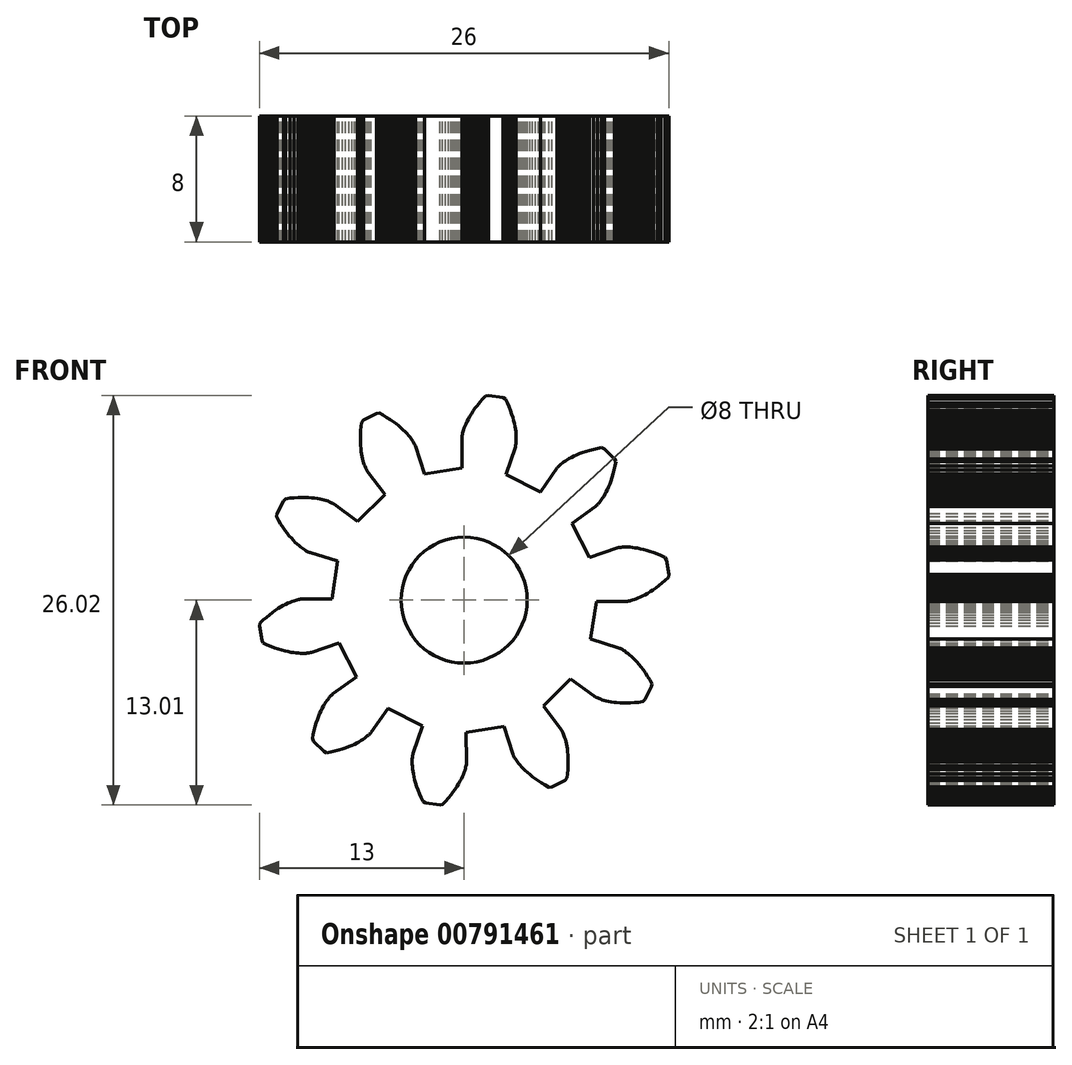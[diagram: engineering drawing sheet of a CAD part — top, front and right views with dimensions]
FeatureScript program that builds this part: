
annotation { "Feature Type Name" : "Feature", "Feature Type Description" : "" }
export const myFeature = defineFeature(function(context is Context, id is Id, definition is map)
    precondition{}
    {
        {
            var Q0;
            Q0=qCreatedBy(makeId("Front.planeOp"),FACE);
            var sketch = newSketch(context, id + "F0", { "sketchPlane" : qUnion([Q0])});
            skCircle(sketch, "E0", {"center": v(0, 0) * mm, "radius": 4 * mm});
            skLineSegment(sketch, "E1", {"start": v(-8.4, 0.07) * mm, "end": v(-10.26, 0.08) * mm});
            skLineSegment(sketch, "E2", {"start": v(-10.26, 0.08) * mm, "end": v(-10.27, 0.08) * mm});
            skLineSegment(sketch, "E3", {"start": v(-10.27, 0.08) * mm, "end": v(-10.3, 0.08) * mm});
            skLineSegment(sketch, "E4", {"start": v(-10.3, 0.08) * mm, "end": v(-10.33, 0.08) * mm});
            skLineSegment(sketch, "E5", {"start": v(-10.33, 0.08) * mm, "end": v(-10.38, 0.07) * mm});
            skLineSegment(sketch, "E6", {"start": v(-10.38, 0.07) * mm, "end": v(-10.45, 0.06) * mm});
            skLineSegment(sketch, "E7", {"start": v(-10.45, 0.06) * mm, "end": v(-10.52, 0.04) * mm});
            skLineSegment(sketch, "E8", {"start": v(-10.52, 0.04) * mm, "end": v(-10.6, 0.02) * mm});
            skLineSegment(sketch, "E9", {"start": v(-10.6, 0.02) * mm, "end": v(-10.7, 0) * mm});
            skLineSegment(sketch, "E10", {"start": v(-10.7, 0) * mm, "end": v(-10.8, -0.04) * mm});
            skLineSegment(sketch, "E11", {"start": v(-10.8, -0.04) * mm, "end": v(-10.93, -0.08) * mm});
            skLineSegment(sketch, "E12", {"start": v(-10.93, -0.08) * mm, "end": v(-11.05, -0.13) * mm});
            skLineSegment(sketch, "E13", {"start": v(-11.05, -0.13) * mm, "end": v(-11.2, -0.2) * mm});
            skLineSegment(sketch, "E14", {"start": v(-11.2, -0.2) * mm, "end": v(-11.34, -0.26) * mm});
            skLineSegment(sketch, "E15", {"start": v(-11.34, -0.26) * mm, "end": v(-11.5, -0.34) * mm});
            skLineSegment(sketch, "E16", {"start": v(-11.5, -0.34) * mm, "end": v(-11.66, -0.43) * mm});
            skLineSegment(sketch, "E17", {"start": v(-11.66, -0.43) * mm, "end": v(-11.83, -0.54) * mm});
            skLineSegment(sketch, "E18", {"start": v(-11.83, -0.54) * mm, "end": v(-12, -0.66) * mm});
            skLineSegment(sketch, "E19", {"start": v(-12, -0.66) * mm, "end": v(-12.19, -0.79) * mm});
            skLineSegment(sketch, "E20", {"start": v(-12.19, -0.79) * mm, "end": v(-12.37, -0.93) * mm});
            skLineSegment(sketch, "E21", {"start": v(-12.37, -0.93) * mm, "end": v(-12.57, -1.1) * mm});
            skLineSegment(sketch, "E22", {"start": v(-12.57, -1.1) * mm, "end": v(-12.76, -1.26) * mm});
            skLineSegment(sketch, "E23", {"start": v(-12.76, -1.26) * mm, "end": v(-12.96, -1.45) * mm});
            skLineSegment(sketch, "E24", {"start": v(-12.96, -1.45) * mm, "end": v(-13, -1.64) * mm});
            skLineSegment(sketch, "E25", {"start": v(-13, -1.64) * mm, "end": v(-12.85, -2.55) * mm});
            skLineSegment(sketch, "E26", {"start": v(-12.85, -2.55) * mm, "end": v(-12.76, -2.71) * mm});
            skLineSegment(sketch, "E27", {"start": v(-12.76, -2.71) * mm, "end": v(-12.51, -2.83) * mm});
            skLineSegment(sketch, "E28", {"start": v(-12.51, -2.83) * mm, "end": v(-12.27, -2.93) * mm});
            skLineSegment(sketch, "E29", {"start": v(-12.27, -2.93) * mm, "end": v(-12.04, -3.02) * mm});
            skLineSegment(sketch, "E30", {"start": v(-12.04, -3.02) * mm, "end": v(-11.81, -3.1) * mm});
            skLineSegment(sketch, "E31", {"start": v(-11.81, -3.1) * mm, "end": v(-11.6, -3.17) * mm});
            skLineSegment(sketch, "E32", {"start": v(-11.6, -3.17) * mm, "end": v(-11.4, -3.22) * mm});
            skLineSegment(sketch, "E33", {"start": v(-11.4, -3.22) * mm, "end": v(-11.2, -3.27) * mm});
            skLineSegment(sketch, "E34", {"start": v(-11.2, -3.27) * mm, "end": v(-11.01, -3.3) * mm});
            skLineSegment(sketch, "E35", {"start": v(-11.01, -3.3) * mm, "end": v(-10.84, -3.33) * mm});
            skLineSegment(sketch, "E36", {"start": v(-10.84, -3.33) * mm, "end": v(-10.68, -3.35) * mm});
            skLineSegment(sketch, "E37", {"start": v(-10.68, -3.35) * mm, "end": v(-10.53, -3.37) * mm});
            skLineSegment(sketch, "E38", {"start": v(-10.53, -3.37) * mm, "end": v(-10.4, -3.37) * mm});
            skLineSegment(sketch, "E39", {"start": v(-10.4, -3.37) * mm, "end": v(-10.27, -3.38) * mm});
            skLineSegment(sketch, "E40", {"start": v(-10.27, -3.38) * mm, "end": v(-10.15, -3.37) * mm});
            skLineSegment(sketch, "E41", {"start": v(-10.15, -3.37) * mm, "end": v(-10.05, -3.37) * mm});
            skLineSegment(sketch, "E42", {"start": v(-10.05, -3.37) * mm, "end": v(-9.97, -3.36) * mm});
            skLineSegment(sketch, "E43", {"start": v(-9.97, -3.36) * mm, "end": v(-9.9, -3.35) * mm});
            skLineSegment(sketch, "E44", {"start": v(-9.9, -3.35) * mm, "end": v(-9.83, -3.34) * mm});
            skLineSegment(sketch, "E45", {"start": v(-9.83, -3.34) * mm, "end": v(-9.78, -3.33) * mm});
            skLineSegment(sketch, "E46", {"start": v(-9.78, -3.33) * mm, "end": v(-9.75, -3.33) * mm});
            skLineSegment(sketch, "E47", {"start": v(-9.75, -3.33) * mm, "end": v(-9.72, -3.32) * mm});
            skLineSegment(sketch, "E48", {"start": v(-9.72, -3.32) * mm, "end": v(-9.7, -3.32) * mm});
            skLineSegment(sketch, "E49", {"start": v(-9.7, -3.32) * mm, "end": v(-7.95, -2.72) * mm});
            skLineSegment(sketch, "E50", {"start": v(-7.95, -2.72) * mm, "end": v(-6.84, -4.89) * mm});
            skLineSegment(sketch, "E51", {"start": v(-6.84, -4.89) * mm, "end": v(-8.35, -5.96) * mm});
            skLineSegment(sketch, "E52", {"start": v(-8.35, -5.96) * mm, "end": v(-8.36, -5.97) * mm});
            skLineSegment(sketch, "E53", {"start": v(-8.36, -5.97) * mm, "end": v(-8.38, -5.99) * mm});
            skLineSegment(sketch, "E54", {"start": v(-8.38, -5.99) * mm, "end": v(-8.4, -6.01) * mm});
            skLineSegment(sketch, "E55", {"start": v(-8.4, -6.01) * mm, "end": v(-8.44, -6.05) * mm});
            skLineSegment(sketch, "E56", {"start": v(-8.44, -6.05) * mm, "end": v(-8.48, -6.1) * mm});
            skLineSegment(sketch, "E57", {"start": v(-8.48, -6.1) * mm, "end": v(-8.54, -6.15) * mm});
            skLineSegment(sketch, "E58", {"start": v(-8.54, -6.15) * mm, "end": v(-8.6, -6.21) * mm});
            skLineSegment(sketch, "E59", {"start": v(-8.6, -6.21) * mm, "end": v(-8.65, -6.3) * mm});
            skLineSegment(sketch, "E60", {"start": v(-8.65, -6.3) * mm, "end": v(-8.72, -6.38) * mm});
            skLineSegment(sketch, "E61", {"start": v(-8.72, -6.38) * mm, "end": v(-8.8, -6.49) * mm});
            skLineSegment(sketch, "E62", {"start": v(-8.8, -6.49) * mm, "end": v(-8.87, -6.6) * mm});
            skLineSegment(sketch, "E63", {"start": v(-8.87, -6.6) * mm, "end": v(-8.94, -6.73) * mm});
            skLineSegment(sketch, "E64", {"start": v(-8.94, -6.73) * mm, "end": v(-9.02, -6.87) * mm});
            skLineSegment(sketch, "E65", {"start": v(-9.02, -6.87) * mm, "end": v(-9.1, -7.03) * mm});
            skLineSegment(sketch, "E66", {"start": v(-9.1, -7.03) * mm, "end": v(-9.17, -7.2) * mm});
            skLineSegment(sketch, "E67", {"start": v(-9.17, -7.2) * mm, "end": v(-9.25, -7.39) * mm});
            skLineSegment(sketch, "E68", {"start": v(-9.25, -7.39) * mm, "end": v(-9.33, -7.59) * mm});
            skLineSegment(sketch, "E69", {"start": v(-9.33, -7.59) * mm, "end": v(-9.4, -7.8) * mm});
            skLineSegment(sketch, "E70", {"start": v(-9.4, -7.8) * mm, "end": v(-9.46, -8.03) * mm});
            skLineSegment(sketch, "E71", {"start": v(-9.46, -8.03) * mm, "end": v(-9.53, -8.27) * mm});
            skLineSegment(sketch, "E72", {"start": v(-9.53, -8.27) * mm, "end": v(-9.58, -8.53) * mm});
            skLineSegment(sketch, "E73", {"start": v(-9.58, -8.53) * mm, "end": v(-9.63, -8.8) * mm});
            skLineSegment(sketch, "E74", {"start": v(-9.63, -8.8) * mm, "end": v(-9.55, -8.97) * mm});
            skLineSegment(sketch, "E75", {"start": v(-9.55, -8.97) * mm, "end": v(-8.9, -9.61) * mm});
            skLineSegment(sketch, "E76", {"start": v(-8.9, -9.61) * mm, "end": v(-8.73, -9.7) * mm});
            skLineSegment(sketch, "E77", {"start": v(-8.73, -9.7) * mm, "end": v(-8.46, -9.64) * mm});
            skLineSegment(sketch, "E78", {"start": v(-8.46, -9.64) * mm, "end": v(-8.2, -9.58) * mm});
            skLineSegment(sketch, "E79", {"start": v(-8.2, -9.58) * mm, "end": v(-7.96, -9.52) * mm});
            skLineSegment(sketch, "E80", {"start": v(-7.96, -9.52) * mm, "end": v(-7.73, -9.45) * mm});
            skLineSegment(sketch, "E81", {"start": v(-7.73, -9.45) * mm, "end": v(-7.52, -9.38) * mm});
            skLineSegment(sketch, "E82", {"start": v(-7.52, -9.38) * mm, "end": v(-7.32, -9.3) * mm});
            skLineSegment(sketch, "E83", {"start": v(-7.32, -9.3) * mm, "end": v(-7.14, -9.22) * mm});
            skLineSegment(sketch, "E84", {"start": v(-7.14, -9.22) * mm, "end": v(-6.97, -9.15) * mm});
            skLineSegment(sketch, "E85", {"start": v(-6.97, -9.15) * mm, "end": v(-6.81, -9.07) * mm});
            skLineSegment(sketch, "E86", {"start": v(-6.81, -9.07) * mm, "end": v(-6.67, -8.99) * mm});
            skLineSegment(sketch, "E87", {"start": v(-6.67, -8.99) * mm, "end": v(-6.54, -8.91) * mm});
            skLineSegment(sketch, "E88", {"start": v(-6.54, -8.91) * mm, "end": v(-6.42, -8.84) * mm});
            skLineSegment(sketch, "E89", {"start": v(-6.42, -8.84) * mm, "end": v(-6.32, -8.77) * mm});
            skLineSegment(sketch, "E90", {"start": v(-6.32, -8.77) * mm, "end": v(-6.23, -8.7) * mm});
            skLineSegment(sketch, "E91", {"start": v(-6.23, -8.7) * mm, "end": v(-6.15, -8.64) * mm});
            skLineSegment(sketch, "E92", {"start": v(-6.15, -8.64) * mm, "end": v(-6.09, -8.58) * mm});
            skLineSegment(sketch, "E93", {"start": v(-6.09, -8.58) * mm, "end": v(-6.03, -8.53) * mm});
            skLineSegment(sketch, "E94", {"start": v(-6.03, -8.53) * mm, "end": v(-5.99, -8.48) * mm});
            skLineSegment(sketch, "E95", {"start": v(-5.99, -8.48) * mm, "end": v(-5.95, -8.45) * mm});
            skLineSegment(sketch, "E96", {"start": v(-5.95, -8.45) * mm, "end": v(-5.93, -8.42) * mm});
            skLineSegment(sketch, "E97", {"start": v(-5.93, -8.42) * mm, "end": v(-5.91, -8.4) * mm});
            skLineSegment(sketch, "E98", {"start": v(-5.91, -8.4) * mm, "end": v(-5.9, -8.39) * mm});
            skLineSegment(sketch, "E99", {"start": v(-5.9, -8.39) * mm, "end": v(-4.84, -6.87) * mm});
            skLineSegment(sketch, "E100", {"start": v(-4.84, -6.87) * mm, "end": v(-2.66, -7.97) * mm});
            skLineSegment(sketch, "E101", {"start": v(-2.66, -7.97) * mm, "end": v(-3.25, -9.73) * mm});
            skLineSegment(sketch, "E102", {"start": v(-3.25, -9.73) * mm, "end": v(-3.25, -9.74) * mm});
            skLineSegment(sketch, "E103", {"start": v(-3.25, -9.74) * mm, "end": v(-3.26, -9.77) * mm});
            skLineSegment(sketch, "E104", {"start": v(-3.26, -9.77) * mm, "end": v(-3.27, -9.8) * mm});
            skLineSegment(sketch, "E105", {"start": v(-3.27, -9.8) * mm, "end": v(-3.27, -9.85) * mm});
            skLineSegment(sketch, "E106", {"start": v(-3.27, -9.85) * mm, "end": v(-3.28, -9.92) * mm});
            skLineSegment(sketch, "E107", {"start": v(-3.28, -9.92) * mm, "end": v(-3.3, -10) * mm});
            skLineSegment(sketch, "E108", {"start": v(-3.3, -10) * mm, "end": v(-3.3, -10.08) * mm});
            skLineSegment(sketch, "E109", {"start": v(-3.3, -10.08) * mm, "end": v(-3.3, -10.18) * mm});
            skLineSegment(sketch, "E110", {"start": v(-3.3, -10.18) * mm, "end": v(-3.3, -10.3) * mm});
            skLineSegment(sketch, "E111", {"start": v(-3.3, -10.3) * mm, "end": v(-3.3, -10.42) * mm});
            skLineSegment(sketch, "E112", {"start": v(-3.3, -10.42) * mm, "end": v(-3.3, -10.55) * mm});
            skLineSegment(sketch, "E113", {"start": v(-3.3, -10.55) * mm, "end": v(-3.28, -10.7) * mm});
            skLineSegment(sketch, "E114", {"start": v(-3.28, -10.7) * mm, "end": v(-3.26, -10.86) * mm});
            skLineSegment(sketch, "E115", {"start": v(-3.26, -10.86) * mm, "end": v(-3.23, -11.04) * mm});
            skLineSegment(sketch, "E116", {"start": v(-3.23, -11.04) * mm, "end": v(-3.19, -11.22) * mm});
            skLineSegment(sketch, "E117", {"start": v(-3.19, -11.22) * mm, "end": v(-3.14, -11.41) * mm});
            skLineSegment(sketch, "E118", {"start": v(-3.14, -11.41) * mm, "end": v(-3.09, -11.62) * mm});
            skLineSegment(sketch, "E119", {"start": v(-3.09, -11.62) * mm, "end": v(-3.02, -11.83) * mm});
            skLineSegment(sketch, "E120", {"start": v(-3.02, -11.83) * mm, "end": v(-2.94, -12.06) * mm});
            skLineSegment(sketch, "E121", {"start": v(-2.94, -12.06) * mm, "end": v(-2.85, -12.29) * mm});
            skLineSegment(sketch, "E122", {"start": v(-2.85, -12.29) * mm, "end": v(-2.74, -12.53) * mm});
            skLineSegment(sketch, "E123", {"start": v(-2.74, -12.53) * mm, "end": v(-2.62, -12.78) * mm});
            skLineSegment(sketch, "E124", {"start": v(-2.62, -12.78) * mm, "end": v(-2.46, -12.87) * mm});
            skLineSegment(sketch, "E125", {"start": v(-2.46, -12.87) * mm, "end": v(-1.55, -13) * mm});
            skLineSegment(sketch, "E126", {"start": v(-1.55, -13) * mm, "end": v(-1.36, -12.97) * mm});
            skLineSegment(sketch, "E127", {"start": v(-1.36, -12.97) * mm, "end": v(-1.18, -12.77) * mm});
            skLineSegment(sketch, "E128", {"start": v(-1.18, -12.77) * mm, "end": v(-1, -12.57) * mm});
            skLineSegment(sketch, "E129", {"start": v(-1, -12.57) * mm, "end": v(-0.84, -12.38) * mm});
            skLineSegment(sketch, "E130", {"start": v(-0.84, -12.38) * mm, "end": v(-0.7, -12.2) * mm});
            skLineSegment(sketch, "E131", {"start": v(-0.7, -12.2) * mm, "end": v(-0.57, -12) * mm});
            skLineSegment(sketch, "E132", {"start": v(-0.57, -12) * mm, "end": v(-0.46, -11.83) * mm});
            skLineSegment(sketch, "E133", {"start": v(-0.46, -11.83) * mm, "end": v(-0.35, -11.66) * mm});
            skLineSegment(sketch, "E134", {"start": v(-0.35, -11.66) * mm, "end": v(-0.26, -11.5) * mm});
            skLineSegment(sketch, "E135", {"start": v(-0.26, -11.5) * mm, "end": v(-0.18, -11.34) * mm});
            skLineSegment(sketch, "E136", {"start": v(-0.18, -11.34) * mm, "end": v(-0.11, -11.2) * mm});
            skLineSegment(sketch, "E137", {"start": v(-0.11, -11.2) * mm, "end": v(-0.05, -11.05) * mm});
            skLineSegment(sketch, "E138", {"start": v(-0.05, -11.05) * mm, "end": v(0, -10.93) * mm});
            skLineSegment(sketch, "E139", {"start": v(0, -10.93) * mm, "end": v(0.04, -10.8) * mm});
            skLineSegment(sketch, "E140", {"start": v(0.04, -10.8) * mm, "end": v(0.07, -10.7) * mm});
            skLineSegment(sketch, "E141", {"start": v(0.07, -10.7) * mm, "end": v(0.1, -10.6) * mm});
            skLineSegment(sketch, "E142", {"start": v(0.1, -10.6) * mm, "end": v(0.12, -10.52) * mm});
            skLineSegment(sketch, "E143", {"start": v(0.12, -10.52) * mm, "end": v(0.13, -10.44) * mm});
            skLineSegment(sketch, "E144", {"start": v(0.13, -10.44) * mm, "end": v(0.14, -10.38) * mm});
            skLineSegment(sketch, "E145", {"start": v(0.14, -10.38) * mm, "end": v(0.15, -10.33) * mm});
            skLineSegment(sketch, "E146", {"start": v(0.15, -10.33) * mm, "end": v(0.15, -10.3) * mm});
            skLineSegment(sketch, "E147", {"start": v(0.15, -10.3) * mm, "end": v(0.15, -10.27) * mm});
            skLineSegment(sketch, "E148", {"start": v(0.15, -10.27) * mm, "end": v(0.15, -10.26) * mm});
            skLineSegment(sketch, "E149", {"start": v(0.15, -10.26) * mm, "end": v(0.13, -8.4) * mm});
            skLineSegment(sketch, "E150", {"start": v(0.13, -8.4) * mm, "end": v(2.53, -8.01) * mm});
            skLineSegment(sketch, "E151", {"start": v(2.53, -8.01) * mm, "end": v(3.1, -9.78) * mm});
            skLineSegment(sketch, "E152", {"start": v(3.1, -9.78) * mm, "end": v(3.1, -9.8) * mm});
            skLineSegment(sketch, "E153", {"start": v(3.1, -9.8) * mm, "end": v(3.1, -9.82) * mm});
            skLineSegment(sketch, "E154", {"start": v(3.1, -9.82) * mm, "end": v(3.12, -9.85) * mm});
            skLineSegment(sketch, "E155", {"start": v(3.12, -9.85) * mm, "end": v(3.14, -9.9) * mm});
            skLineSegment(sketch, "E156", {"start": v(3.14, -9.9) * mm, "end": v(3.17, -9.95) * mm});
            skLineSegment(sketch, "E157", {"start": v(3.17, -9.95) * mm, "end": v(3.2, -10.02) * mm});
            skLineSegment(sketch, "E158", {"start": v(3.2, -10.02) * mm, "end": v(3.26, -10.1) * mm});
            skLineSegment(sketch, "E159", {"start": v(3.26, -10.1) * mm, "end": v(3.31, -10.18) * mm});
            skLineSegment(sketch, "E160", {"start": v(3.31, -10.18) * mm, "end": v(3.38, -10.27) * mm});
            skLineSegment(sketch, "E161", {"start": v(3.38, -10.27) * mm, "end": v(3.45, -10.37) * mm});
            skLineSegment(sketch, "E162", {"start": v(3.45, -10.37) * mm, "end": v(3.54, -10.47) * mm});
            skLineSegment(sketch, "E163", {"start": v(3.54, -10.47) * mm, "end": v(3.64, -10.58) * mm});
            skLineSegment(sketch, "E164", {"start": v(3.64, -10.58) * mm, "end": v(3.75, -10.7) * mm});
            skLineSegment(sketch, "E165", {"start": v(3.75, -10.7) * mm, "end": v(3.88, -10.82) * mm});
            skLineSegment(sketch, "E166", {"start": v(3.88, -10.82) * mm, "end": v(4.01, -10.95) * mm});
            skLineSegment(sketch, "E167", {"start": v(4.01, -10.95) * mm, "end": v(4.17, -11.08) * mm});
            skLineSegment(sketch, "E168", {"start": v(4.17, -11.08) * mm, "end": v(4.33, -11.21) * mm});
            skLineSegment(sketch, "E169", {"start": v(4.33, -11.21) * mm, "end": v(4.51, -11.35) * mm});
            skLineSegment(sketch, "E170", {"start": v(4.51, -11.35) * mm, "end": v(4.7, -11.48) * mm});
            skLineSegment(sketch, "E171", {"start": v(4.7, -11.48) * mm, "end": v(4.92, -11.61) * mm});
            skLineSegment(sketch, "E172", {"start": v(4.92, -11.61) * mm, "end": v(5.15, -11.75) * mm});
            skLineSegment(sketch, "E173", {"start": v(5.15, -11.75) * mm, "end": v(5.39, -11.88) * mm});
            skLineSegment(sketch, "E174", {"start": v(5.39, -11.88) * mm, "end": v(5.57, -11.85) * mm});
            skLineSegment(sketch, "E175", {"start": v(5.57, -11.85) * mm, "end": v(6.4, -11.43) * mm});
            skLineSegment(sketch, "E176", {"start": v(6.4, -11.43) * mm, "end": v(6.52, -11.3) * mm});
            skLineSegment(sketch, "E177", {"start": v(6.52, -11.3) * mm, "end": v(6.56, -11.02) * mm});
            skLineSegment(sketch, "E178", {"start": v(6.56, -11.02) * mm, "end": v(6.58, -10.76) * mm});
            skLineSegment(sketch, "E179", {"start": v(6.58, -10.76) * mm, "end": v(6.6, -10.51) * mm});
            skLineSegment(sketch, "E180", {"start": v(6.6, -10.51) * mm, "end": v(6.6, -10.28) * mm});
            skLineSegment(sketch, "E181", {"start": v(6.6, -10.28) * mm, "end": v(6.6, -10.05) * mm});
            skLineSegment(sketch, "E182", {"start": v(6.6, -10.05) * mm, "end": v(6.58, -9.84) * mm});
            skLineSegment(sketch, "E183", {"start": v(6.58, -9.84) * mm, "end": v(6.57, -9.64) * mm});
            skLineSegment(sketch, "E184", {"start": v(6.57, -9.64) * mm, "end": v(6.55, -9.45) * mm});
            skLineSegment(sketch, "E185", {"start": v(6.55, -9.45) * mm, "end": v(6.52, -9.28) * mm});
            skLineSegment(sketch, "E186", {"start": v(6.52, -9.28) * mm, "end": v(6.49, -9.12) * mm});
            skLineSegment(sketch, "E187", {"start": v(6.49, -9.12) * mm, "end": v(6.45, -8.97) * mm});
            skLineSegment(sketch, "E188", {"start": v(6.45, -8.97) * mm, "end": v(6.42, -8.84) * mm});
            skLineSegment(sketch, "E189", {"start": v(6.42, -8.84) * mm, "end": v(6.38, -8.72) * mm});
            skLineSegment(sketch, "E190", {"start": v(6.38, -8.72) * mm, "end": v(6.35, -8.61) * mm});
            skLineSegment(sketch, "E191", {"start": v(6.35, -8.61) * mm, "end": v(6.31, -8.52) * mm});
            skLineSegment(sketch, "E192", {"start": v(6.31, -8.52) * mm, "end": v(6.28, -8.44) * mm});
            skLineSegment(sketch, "E193", {"start": v(6.28, -8.44) * mm, "end": v(6.25, -8.37) * mm});
            skLineSegment(sketch, "E194", {"start": v(6.25, -8.37) * mm, "end": v(6.22, -8.32) * mm});
            skLineSegment(sketch, "E195", {"start": v(6.22, -8.32) * mm, "end": v(6.2, -8.27) * mm});
            skLineSegment(sketch, "E196", {"start": v(6.2, -8.27) * mm, "end": v(6.17, -8.24) * mm});
            skLineSegment(sketch, "E197", {"start": v(6.17, -8.24) * mm, "end": v(6.16, -8.22) * mm});
            skLineSegment(sketch, "E198", {"start": v(6.16, -8.22) * mm, "end": v(6.15, -8.2) * mm});
            skLineSegment(sketch, "E199", {"start": v(6.15, -8.2) * mm, "end": v(5.04, -6.73) * mm});
            skLineSegment(sketch, "E200", {"start": v(5.04, -6.73) * mm, "end": v(6.76, -5) * mm});
            skLineSegment(sketch, "E201", {"start": v(6.76, -5) * mm, "end": v(8.25, -6.1) * mm});
            skLineSegment(sketch, "E202", {"start": v(8.25, -6.1) * mm, "end": v(8.26, -6.1) * mm});
            skLineSegment(sketch, "E203", {"start": v(8.26, -6.1) * mm, "end": v(8.28, -6.12) * mm});
            skLineSegment(sketch, "E204", {"start": v(8.28, -6.12) * mm, "end": v(8.32, -6.14) * mm});
            skLineSegment(sketch, "E205", {"start": v(8.32, -6.14) * mm, "end": v(8.36, -6.16) * mm});
            skLineSegment(sketch, "E206", {"start": v(8.36, -6.16) * mm, "end": v(8.42, -6.19) * mm});
            skLineSegment(sketch, "E207", {"start": v(8.42, -6.19) * mm, "end": v(8.48, -6.22) * mm});
            skLineSegment(sketch, "E208", {"start": v(8.48, -6.22) * mm, "end": v(8.57, -6.25) * mm});
            skLineSegment(sketch, "E209", {"start": v(8.57, -6.25) * mm, "end": v(8.66, -6.29) * mm});
            skLineSegment(sketch, "E210", {"start": v(8.66, -6.29) * mm, "end": v(8.77, -6.32) * mm});
            skLineSegment(sketch, "E211", {"start": v(8.77, -6.32) * mm, "end": v(8.89, -6.36) * mm});
            skLineSegment(sketch, "E212", {"start": v(8.89, -6.36) * mm, "end": v(9.02, -6.4) * mm});
            skLineSegment(sketch, "E213", {"start": v(9.02, -6.4) * mm, "end": v(9.17, -6.42) * mm});
            skLineSegment(sketch, "E214", {"start": v(9.17, -6.42) * mm, "end": v(9.33, -6.45) * mm});
            skLineSegment(sketch, "E215", {"start": v(9.33, -6.45) * mm, "end": v(9.5, -6.48) * mm});
            skLineSegment(sketch, "E216", {"start": v(9.5, -6.48) * mm, "end": v(9.68, -6.5) * mm});
            skLineSegment(sketch, "E217", {"start": v(9.68, -6.5) * mm, "end": v(9.88, -6.52) * mm});
            skLineSegment(sketch, "E218", {"start": v(9.88, -6.52) * mm, "end": v(10.1, -6.52) * mm});
            skLineSegment(sketch, "E219", {"start": v(10.1, -6.52) * mm, "end": v(10.32, -6.53) * mm});
            skLineSegment(sketch, "E220", {"start": v(10.32, -6.53) * mm, "end": v(10.56, -6.52) * mm});
            skLineSegment(sketch, "E221", {"start": v(10.56, -6.52) * mm, "end": v(10.8, -6.5) * mm});
            skLineSegment(sketch, "E222", {"start": v(10.8, -6.5) * mm, "end": v(11.07, -6.48) * mm});
            skLineSegment(sketch, "E223", {"start": v(11.07, -6.48) * mm, "end": v(11.34, -6.44) * mm});
            skLineSegment(sketch, "E224", {"start": v(11.34, -6.44) * mm, "end": v(11.48, -6.31) * mm});
            skLineSegment(sketch, "E225", {"start": v(11.48, -6.31) * mm, "end": v(11.9, -5.5) * mm});
            skLineSegment(sketch, "E226", {"start": v(11.9, -5.5) * mm, "end": v(11.92, -5.3) * mm});
            skLineSegment(sketch, "E227", {"start": v(11.92, -5.3) * mm, "end": v(11.78, -5.06) * mm});
            skLineSegment(sketch, "E228", {"start": v(11.78, -5.06) * mm, "end": v(11.65, -4.84) * mm});
            skLineSegment(sketch, "E229", {"start": v(11.65, -4.84) * mm, "end": v(11.51, -4.63) * mm});
            skLineSegment(sketch, "E230", {"start": v(11.51, -4.63) * mm, "end": v(11.38, -4.43) * mm});
            skLineSegment(sketch, "E231", {"start": v(11.38, -4.43) * mm, "end": v(11.24, -4.25) * mm});
            skLineSegment(sketch, "E232", {"start": v(11.24, -4.25) * mm, "end": v(11.1, -4.09) * mm});
            skLineSegment(sketch, "E233", {"start": v(11.1, -4.09) * mm, "end": v(10.98, -3.94) * mm});
            skLineSegment(sketch, "E234", {"start": v(10.98, -3.94) * mm, "end": v(10.85, -3.8) * mm});
            skLineSegment(sketch, "E235", {"start": v(10.85, -3.8) * mm, "end": v(10.73, -3.68) * mm});
            skLineSegment(sketch, "E236", {"start": v(10.73, -3.68) * mm, "end": v(10.6, -3.56) * mm});
            skLineSegment(sketch, "E237", {"start": v(10.6, -3.56) * mm, "end": v(10.5, -3.47) * mm});
            skLineSegment(sketch, "E238", {"start": v(10.5, -3.47) * mm, "end": v(10.39, -3.38) * mm});
            skLineSegment(sketch, "E239", {"start": v(10.39, -3.38) * mm, "end": v(10.3, -3.3) * mm});
            skLineSegment(sketch, "E240", {"start": v(10.3, -3.3) * mm, "end": v(10.2, -3.24) * mm});
            skLineSegment(sketch, "E241", {"start": v(10.2, -3.24) * mm, "end": v(10.11, -3.18) * mm});
            skLineSegment(sketch, "E242", {"start": v(10.11, -3.18) * mm, "end": v(10.04, -3.14) * mm});
            skLineSegment(sketch, "E243", {"start": v(10.04, -3.14) * mm, "end": v(9.97, -3.1) * mm});
            skLineSegment(sketch, "E244", {"start": v(9.97, -3.1) * mm, "end": v(9.92, -3.07) * mm});
            skLineSegment(sketch, "E245", {"start": v(9.92, -3.07) * mm, "end": v(9.87, -3.05) * mm});
            skLineSegment(sketch, "E246", {"start": v(9.87, -3.05) * mm, "end": v(9.84, -3.04) * mm});
            skLineSegment(sketch, "E247", {"start": v(9.84, -3.04) * mm, "end": v(9.82, -3.03) * mm});
            skLineSegment(sketch, "E248", {"start": v(9.82, -3.03) * mm, "end": v(9.8, -3.02) * mm});
            skLineSegment(sketch, "E249", {"start": v(9.8, -3.02) * mm, "end": v(8.03, -2.48) * mm});
            skLineSegment(sketch, "E250", {"start": v(8.03, -2.48) * mm, "end": v(8.4, -0.07) * mm});
            skLineSegment(sketch, "E251", {"start": v(8.4, -0.07) * mm, "end": v(10.26, -0.08) * mm});
            skLineSegment(sketch, "E252", {"start": v(10.26, -0.08) * mm, "end": v(10.27, -0.08) * mm});
            skLineSegment(sketch, "E253", {"start": v(10.27, -0.08) * mm, "end": v(10.3, -0.08) * mm});
            skLineSegment(sketch, "E254", {"start": v(10.3, -0.08) * mm, "end": v(10.33, -0.08) * mm});
            skLineSegment(sketch, "E255", {"start": v(10.33, -0.08) * mm, "end": v(10.38, -0.07) * mm});
            skLineSegment(sketch, "E256", {"start": v(10.38, -0.07) * mm, "end": v(10.45, -0.06) * mm});
            skLineSegment(sketch, "E257", {"start": v(10.45, -0.06) * mm, "end": v(10.52, -0.04) * mm});
            skLineSegment(sketch, "E258", {"start": v(10.52, -0.04) * mm, "end": v(10.6, -0.02) * mm});
            skLineSegment(sketch, "E259", {"start": v(10.6, -0.02) * mm, "end": v(10.7, 0) * mm});
            skLineSegment(sketch, "E260", {"start": v(10.7, 0) * mm, "end": v(10.8, 0.04) * mm});
            skLineSegment(sketch, "E261", {"start": v(10.8, 0.04) * mm, "end": v(10.93, 0.08) * mm});
            skLineSegment(sketch, "E262", {"start": v(10.93, 0.08) * mm, "end": v(11.05, 0.13) * mm});
            skLineSegment(sketch, "E263", {"start": v(11.05, 0.13) * mm, "end": v(11.2, 0.2) * mm});
            skLineSegment(sketch, "E264", {"start": v(11.2, 0.2) * mm, "end": v(11.34, 0.26) * mm});
            skLineSegment(sketch, "E265", {"start": v(11.34, 0.26) * mm, "end": v(11.5, 0.34) * mm});
            skLineSegment(sketch, "E266", {"start": v(11.5, 0.34) * mm, "end": v(11.66, 0.43) * mm});
            skLineSegment(sketch, "E267", {"start": v(11.66, 0.43) * mm, "end": v(11.83, 0.54) * mm});
            skLineSegment(sketch, "E268", {"start": v(11.83, 0.54) * mm, "end": v(12, 0.66) * mm});
            skLineSegment(sketch, "E269", {"start": v(12, 0.66) * mm, "end": v(12.19, 0.79) * mm});
            skLineSegment(sketch, "E270", {"start": v(12.19, 0.79) * mm, "end": v(12.37, 0.93) * mm});
            skLineSegment(sketch, "E271", {"start": v(12.37, 0.93) * mm, "end": v(12.57, 1.1) * mm});
            skLineSegment(sketch, "E272", {"start": v(12.57, 1.1) * mm, "end": v(12.76, 1.26) * mm});
            skLineSegment(sketch, "E273", {"start": v(12.76, 1.26) * mm, "end": v(12.96, 1.45) * mm});
            skLineSegment(sketch, "E274", {"start": v(12.96, 1.45) * mm, "end": v(13, 1.64) * mm});
            skLineSegment(sketch, "E275", {"start": v(13, 1.64) * mm, "end": v(12.85, 2.55) * mm});
            skLineSegment(sketch, "E276", {"start": v(12.85, 2.55) * mm, "end": v(12.76, 2.71) * mm});
            skLineSegment(sketch, "E277", {"start": v(12.76, 2.71) * mm, "end": v(12.51, 2.83) * mm});
            skLineSegment(sketch, "E278", {"start": v(12.51, 2.83) * mm, "end": v(12.27, 2.93) * mm});
            skLineSegment(sketch, "E279", {"start": v(12.27, 2.93) * mm, "end": v(12.04, 3.02) * mm});
            skLineSegment(sketch, "E280", {"start": v(12.04, 3.02) * mm, "end": v(11.81, 3.1) * mm});
            skLineSegment(sketch, "E281", {"start": v(11.81, 3.1) * mm, "end": v(11.6, 3.17) * mm});
            skLineSegment(sketch, "E282", {"start": v(11.6, 3.17) * mm, "end": v(11.4, 3.22) * mm});
            skLineSegment(sketch, "E283", {"start": v(11.4, 3.22) * mm, "end": v(11.2, 3.27) * mm});
            skLineSegment(sketch, "E284", {"start": v(11.2, 3.27) * mm, "end": v(11.01, 3.3) * mm});
            skLineSegment(sketch, "E285", {"start": v(11.01, 3.3) * mm, "end": v(10.84, 3.33) * mm});
            skLineSegment(sketch, "E286", {"start": v(10.84, 3.33) * mm, "end": v(10.68, 3.35) * mm});
            skLineSegment(sketch, "E287", {"start": v(10.68, 3.35) * mm, "end": v(10.53, 3.37) * mm});
            skLineSegment(sketch, "E288", {"start": v(10.53, 3.37) * mm, "end": v(10.4, 3.37) * mm});
            skLineSegment(sketch, "E289", {"start": v(10.4, 3.37) * mm, "end": v(10.27, 3.38) * mm});
            skLineSegment(sketch, "E290", {"start": v(10.27, 3.38) * mm, "end": v(10.15, 3.37) * mm});
            skLineSegment(sketch, "E291", {"start": v(10.15, 3.37) * mm, "end": v(10.05, 3.37) * mm});
            skLineSegment(sketch, "E292", {"start": v(10.05, 3.37) * mm, "end": v(9.97, 3.36) * mm});
            skLineSegment(sketch, "E293", {"start": v(9.97, 3.36) * mm, "end": v(9.9, 3.35) * mm});
            skLineSegment(sketch, "E294", {"start": v(9.9, 3.35) * mm, "end": v(9.83, 3.34) * mm});
            skLineSegment(sketch, "E295", {"start": v(9.83, 3.34) * mm, "end": v(9.78, 3.33) * mm});
            skLineSegment(sketch, "E296", {"start": v(9.78, 3.33) * mm, "end": v(9.75, 3.33) * mm});
            skLineSegment(sketch, "E297", {"start": v(9.75, 3.33) * mm, "end": v(9.72, 3.32) * mm});
            skLineSegment(sketch, "E298", {"start": v(9.72, 3.32) * mm, "end": v(9.7, 3.32) * mm});
            skLineSegment(sketch, "E299", {"start": v(9.7, 3.32) * mm, "end": v(7.95, 2.72) * mm});
            skLineSegment(sketch, "E300", {"start": v(7.95, 2.72) * mm, "end": v(6.84, 4.89) * mm});
            skLineSegment(sketch, "E301", {"start": v(6.84, 4.89) * mm, "end": v(8.35, 5.96) * mm});
            skLineSegment(sketch, "E302", {"start": v(8.35, 5.96) * mm, "end": v(8.36, 5.97) * mm});
            skLineSegment(sketch, "E303", {"start": v(8.36, 5.97) * mm, "end": v(8.38, 5.99) * mm});
            skLineSegment(sketch, "E304", {"start": v(8.38, 5.99) * mm, "end": v(8.4, 6.01) * mm});
            skLineSegment(sketch, "E305", {"start": v(8.4, 6.01) * mm, "end": v(8.44, 6.05) * mm});
            skLineSegment(sketch, "E306", {"start": v(8.44, 6.05) * mm, "end": v(8.48, 6.1) * mm});
            skLineSegment(sketch, "E307", {"start": v(8.48, 6.1) * mm, "end": v(8.54, 6.15) * mm});
            skLineSegment(sketch, "E308", {"start": v(8.54, 6.15) * mm, "end": v(8.6, 6.21) * mm});
            skLineSegment(sketch, "E309", {"start": v(8.6, 6.21) * mm, "end": v(8.65, 6.3) * mm});
            skLineSegment(sketch, "E310", {"start": v(8.65, 6.3) * mm, "end": v(8.72, 6.38) * mm});
            skLineSegment(sketch, "E311", {"start": v(8.72, 6.38) * mm, "end": v(8.8, 6.49) * mm});
            skLineSegment(sketch, "E312", {"start": v(8.8, 6.49) * mm, "end": v(8.87, 6.6) * mm});
            skLineSegment(sketch, "E313", {"start": v(8.87, 6.6) * mm, "end": v(8.94, 6.73) * mm});
            skLineSegment(sketch, "E314", {"start": v(8.94, 6.73) * mm, "end": v(9.02, 6.87) * mm});
            skLineSegment(sketch, "E315", {"start": v(9.02, 6.87) * mm, "end": v(9.1, 7.03) * mm});
            skLineSegment(sketch, "E316", {"start": v(9.1, 7.03) * mm, "end": v(9.17, 7.2) * mm});
            skLineSegment(sketch, "E317", {"start": v(9.17, 7.2) * mm, "end": v(9.25, 7.39) * mm});
            skLineSegment(sketch, "E318", {"start": v(9.25, 7.39) * mm, "end": v(9.33, 7.59) * mm});
            skLineSegment(sketch, "E319", {"start": v(9.33, 7.59) * mm, "end": v(9.4, 7.8) * mm});
            skLineSegment(sketch, "E320", {"start": v(9.4, 7.8) * mm, "end": v(9.46, 8.03) * mm});
            skLineSegment(sketch, "E321", {"start": v(9.46, 8.03) * mm, "end": v(9.53, 8.27) * mm});
            skLineSegment(sketch, "E322", {"start": v(9.53, 8.27) * mm, "end": v(9.58, 8.53) * mm});
            skLineSegment(sketch, "E323", {"start": v(9.58, 8.53) * mm, "end": v(9.63, 8.8) * mm});
            skLineSegment(sketch, "E324", {"start": v(9.63, 8.8) * mm, "end": v(9.55, 8.97) * mm});
            skLineSegment(sketch, "E325", {"start": v(9.55, 8.97) * mm, "end": v(8.9, 9.61) * mm});
            skLineSegment(sketch, "E326", {"start": v(8.9, 9.61) * mm, "end": v(8.73, 9.7) * mm});
            skLineSegment(sketch, "E327", {"start": v(8.73, 9.7) * mm, "end": v(8.46, 9.64) * mm});
            skLineSegment(sketch, "E328", {"start": v(8.46, 9.64) * mm, "end": v(8.2, 9.58) * mm});
            skLineSegment(sketch, "E329", {"start": v(8.2, 9.58) * mm, "end": v(7.96, 9.52) * mm});
            skLineSegment(sketch, "E330", {"start": v(7.96, 9.52) * mm, "end": v(7.73, 9.45) * mm});
            skLineSegment(sketch, "E331", {"start": v(7.73, 9.45) * mm, "end": v(7.52, 9.38) * mm});
            skLineSegment(sketch, "E332", {"start": v(7.52, 9.38) * mm, "end": v(7.32, 9.3) * mm});
            skLineSegment(sketch, "E333", {"start": v(7.32, 9.3) * mm, "end": v(7.14, 9.22) * mm});
            skLineSegment(sketch, "E334", {"start": v(7.14, 9.22) * mm, "end": v(6.97, 9.15) * mm});
            skLineSegment(sketch, "E335", {"start": v(6.97, 9.15) * mm, "end": v(6.81, 9.07) * mm});
            skLineSegment(sketch, "E336", {"start": v(6.81, 9.07) * mm, "end": v(6.67, 8.99) * mm});
            skLineSegment(sketch, "E337", {"start": v(6.67, 8.99) * mm, "end": v(6.54, 8.91) * mm});
            skLineSegment(sketch, "E338", {"start": v(6.54, 8.91) * mm, "end": v(6.42, 8.84) * mm});
            skLineSegment(sketch, "E339", {"start": v(6.42, 8.84) * mm, "end": v(6.32, 8.77) * mm});
            skLineSegment(sketch, "E340", {"start": v(6.32, 8.77) * mm, "end": v(6.23, 8.7) * mm});
            skLineSegment(sketch, "E341", {"start": v(6.23, 8.7) * mm, "end": v(6.15, 8.64) * mm});
            skLineSegment(sketch, "E342", {"start": v(6.15, 8.64) * mm, "end": v(6.09, 8.58) * mm});
            skLineSegment(sketch, "E343", {"start": v(6.09, 8.58) * mm, "end": v(6.03, 8.53) * mm});
            skLineSegment(sketch, "E344", {"start": v(6.03, 8.53) * mm, "end": v(5.99, 8.48) * mm});
            skLineSegment(sketch, "E345", {"start": v(5.99, 8.48) * mm, "end": v(5.95, 8.45) * mm});
            skLineSegment(sketch, "E346", {"start": v(5.95, 8.45) * mm, "end": v(5.93, 8.42) * mm});
            skLineSegment(sketch, "E347", {"start": v(5.93, 8.42) * mm, "end": v(5.91, 8.4) * mm});
            skLineSegment(sketch, "E348", {"start": v(5.91, 8.4) * mm, "end": v(5.9, 8.39) * mm});
            skLineSegment(sketch, "E349", {"start": v(5.9, 8.39) * mm, "end": v(4.84, 6.87) * mm});
            skLineSegment(sketch, "E350", {"start": v(4.84, 6.87) * mm, "end": v(2.66, 7.97) * mm});
            skLineSegment(sketch, "E351", {"start": v(2.66, 7.97) * mm, "end": v(3.25, 9.73) * mm});
            skLineSegment(sketch, "E352", {"start": v(3.25, 9.73) * mm, "end": v(3.25, 9.74) * mm});
            skLineSegment(sketch, "E353", {"start": v(3.25, 9.74) * mm, "end": v(3.26, 9.77) * mm});
            skLineSegment(sketch, "E354", {"start": v(3.26, 9.77) * mm, "end": v(3.27, 9.8) * mm});
            skLineSegment(sketch, "E355", {"start": v(3.27, 9.8) * mm, "end": v(3.27, 9.85) * mm});
            skLineSegment(sketch, "E356", {"start": v(3.27, 9.85) * mm, "end": v(3.28, 9.92) * mm});
            skLineSegment(sketch, "E357", {"start": v(3.28, 9.92) * mm, "end": v(3.3, 10) * mm});
            skLineSegment(sketch, "E358", {"start": v(3.3, 10) * mm, "end": v(3.3, 10.08) * mm});
            skLineSegment(sketch, "E359", {"start": v(3.3, 10.08) * mm, "end": v(3.3, 10.18) * mm});
            skLineSegment(sketch, "E360", {"start": v(3.3, 10.18) * mm, "end": v(3.3, 10.3) * mm});
            skLineSegment(sketch, "E361", {"start": v(3.3, 10.3) * mm, "end": v(3.3, 10.42) * mm});
            skLineSegment(sketch, "E362", {"start": v(3.3, 10.42) * mm, "end": v(3.3, 10.55) * mm});
            skLineSegment(sketch, "E363", {"start": v(3.3, 10.55) * mm, "end": v(3.28, 10.7) * mm});
            skLineSegment(sketch, "E364", {"start": v(3.28, 10.7) * mm, "end": v(3.26, 10.86) * mm});
            skLineSegment(sketch, "E365", {"start": v(3.26, 10.86) * mm, "end": v(3.23, 11.04) * mm});
            skLineSegment(sketch, "E366", {"start": v(3.23, 11.04) * mm, "end": v(3.19, 11.22) * mm});
            skLineSegment(sketch, "E367", {"start": v(3.19, 11.22) * mm, "end": v(3.14, 11.41) * mm});
            skLineSegment(sketch, "E368", {"start": v(3.14, 11.41) * mm, "end": v(3.09, 11.62) * mm});
            skLineSegment(sketch, "E369", {"start": v(3.09, 11.62) * mm, "end": v(3.02, 11.83) * mm});
            skLineSegment(sketch, "E370", {"start": v(3.02, 11.83) * mm, "end": v(2.94, 12.06) * mm});
            skLineSegment(sketch, "E371", {"start": v(2.94, 12.06) * mm, "end": v(2.85, 12.29) * mm});
            skLineSegment(sketch, "E372", {"start": v(2.85, 12.29) * mm, "end": v(2.74, 12.53) * mm});
            skLineSegment(sketch, "E373", {"start": v(2.74, 12.53) * mm, "end": v(2.62, 12.78) * mm});
            skLineSegment(sketch, "E374", {"start": v(2.62, 12.78) * mm, "end": v(2.46, 12.87) * mm});
            skLineSegment(sketch, "E375", {"start": v(2.46, 12.87) * mm, "end": v(1.55, 13) * mm});
            skLineSegment(sketch, "E376", {"start": v(1.55, 13) * mm, "end": v(1.36, 12.97) * mm});
            skLineSegment(sketch, "E377", {"start": v(1.36, 12.97) * mm, "end": v(1.18, 12.77) * mm});
            skLineSegment(sketch, "E378", {"start": v(1.18, 12.77) * mm, "end": v(1, 12.57) * mm});
            skLineSegment(sketch, "E379", {"start": v(1, 12.57) * mm, "end": v(0.84, 12.38) * mm});
            skLineSegment(sketch, "E380", {"start": v(0.84, 12.38) * mm, "end": v(0.7, 12.2) * mm});
            skLineSegment(sketch, "E381", {"start": v(0.7, 12.2) * mm, "end": v(0.57, 12) * mm});
            skLineSegment(sketch, "E382", {"start": v(0.57, 12) * mm, "end": v(0.46, 11.83) * mm});
            skLineSegment(sketch, "E383", {"start": v(0.46, 11.83) * mm, "end": v(0.35, 11.66) * mm});
            skLineSegment(sketch, "E384", {"start": v(0.35, 11.66) * mm, "end": v(0.26, 11.5) * mm});
            skLineSegment(sketch, "E385", {"start": v(0.26, 11.5) * mm, "end": v(0.18, 11.34) * mm});
            skLineSegment(sketch, "E386", {"start": v(0.18, 11.34) * mm, "end": v(0.11, 11.2) * mm});
            skLineSegment(sketch, "E387", {"start": v(0.11, 11.2) * mm, "end": v(0.05, 11.05) * mm});
            skLineSegment(sketch, "E388", {"start": v(0.05, 11.05) * mm, "end": v(0, 10.93) * mm});
            skLineSegment(sketch, "E389", {"start": v(0, 10.93) * mm, "end": v(-0.04, 10.8) * mm});
            skLineSegment(sketch, "E390", {"start": v(-0.04, 10.8) * mm, "end": v(-0.07, 10.7) * mm});
            skLineSegment(sketch, "E391", {"start": v(-0.07, 10.7) * mm, "end": v(-0.1, 10.6) * mm});
            skLineSegment(sketch, "E392", {"start": v(-0.1, 10.6) * mm, "end": v(-0.12, 10.52) * mm});
            skLineSegment(sketch, "E393", {"start": v(-0.12, 10.52) * mm, "end": v(-0.13, 10.44) * mm});
            skLineSegment(sketch, "E394", {"start": v(-0.13, 10.44) * mm, "end": v(-0.14, 10.38) * mm});
            skLineSegment(sketch, "E395", {"start": v(-0.14, 10.38) * mm, "end": v(-0.15, 10.33) * mm});
            skLineSegment(sketch, "E396", {"start": v(-0.15, 10.33) * mm, "end": v(-0.15, 10.3) * mm});
            skLineSegment(sketch, "E397", {"start": v(-0.15, 10.3) * mm, "end": v(-0.15, 10.27) * mm});
            skLineSegment(sketch, "E398", {"start": v(-0.15, 10.27) * mm, "end": v(-0.15, 10.26) * mm});
            skLineSegment(sketch, "E399", {"start": v(-0.15, 10.26) * mm, "end": v(-0.13, 8.4) * mm});
            skLineSegment(sketch, "E400", {"start": v(-0.13, 8.4) * mm, "end": v(-2.53, 8.01) * mm});
            skLineSegment(sketch, "E401", {"start": v(-2.53, 8.01) * mm, "end": v(-3.1, 9.78) * mm});
            skLineSegment(sketch, "E402", {"start": v(-3.1, 9.78) * mm, "end": v(-3.1, 9.8) * mm});
            skLineSegment(sketch, "E403", {"start": v(-3.1, 9.8) * mm, "end": v(-3.1, 9.82) * mm});
            skLineSegment(sketch, "E404", {"start": v(-3.1, 9.82) * mm, "end": v(-3.12, 9.85) * mm});
            skLineSegment(sketch, "E405", {"start": v(-3.12, 9.85) * mm, "end": v(-3.14, 9.9) * mm});
            skLineSegment(sketch, "E406", {"start": v(-3.14, 9.9) * mm, "end": v(-3.17, 9.95) * mm});
            skLineSegment(sketch, "E407", {"start": v(-3.17, 9.95) * mm, "end": v(-3.2, 10.02) * mm});
            skLineSegment(sketch, "E408", {"start": v(-3.2, 10.02) * mm, "end": v(-3.26, 10.1) * mm});
            skLineSegment(sketch, "E409", {"start": v(-3.26, 10.1) * mm, "end": v(-3.31, 10.18) * mm});
            skLineSegment(sketch, "E410", {"start": v(-3.31, 10.18) * mm, "end": v(-3.38, 10.27) * mm});
            skLineSegment(sketch, "E411", {"start": v(-3.38, 10.27) * mm, "end": v(-3.45, 10.37) * mm});
            skLineSegment(sketch, "E412", {"start": v(-3.45, 10.37) * mm, "end": v(-3.54, 10.47) * mm});
            skLineSegment(sketch, "E413", {"start": v(-3.54, 10.47) * mm, "end": v(-3.64, 10.58) * mm});
            skLineSegment(sketch, "E414", {"start": v(-3.64, 10.58) * mm, "end": v(-3.75, 10.7) * mm});
            skLineSegment(sketch, "E415", {"start": v(-3.75, 10.7) * mm, "end": v(-3.88, 10.82) * mm});
            skLineSegment(sketch, "E416", {"start": v(-3.88, 10.82) * mm, "end": v(-4.01, 10.95) * mm});
            skLineSegment(sketch, "E417", {"start": v(-4.01, 10.95) * mm, "end": v(-4.17, 11.08) * mm});
            skLineSegment(sketch, "E418", {"start": v(-4.17, 11.08) * mm, "end": v(-4.33, 11.21) * mm});
            skLineSegment(sketch, "E419", {"start": v(-4.33, 11.21) * mm, "end": v(-4.51, 11.35) * mm});
            skLineSegment(sketch, "E420", {"start": v(-4.51, 11.35) * mm, "end": v(-4.7, 11.48) * mm});
            skLineSegment(sketch, "E421", {"start": v(-4.7, 11.48) * mm, "end": v(-4.92, 11.61) * mm});
            skLineSegment(sketch, "E422", {"start": v(-4.92, 11.61) * mm, "end": v(-5.15, 11.75) * mm});
            skLineSegment(sketch, "E423", {"start": v(-5.15, 11.75) * mm, "end": v(-5.39, 11.88) * mm});
            skLineSegment(sketch, "E424", {"start": v(-5.39, 11.88) * mm, "end": v(-5.57, 11.85) * mm});
            skLineSegment(sketch, "E425", {"start": v(-5.57, 11.85) * mm, "end": v(-6.4, 11.43) * mm});
            skLineSegment(sketch, "E426", {"start": v(-6.4, 11.43) * mm, "end": v(-6.52, 11.3) * mm});
            skLineSegment(sketch, "E427", {"start": v(-6.52, 11.3) * mm, "end": v(-6.56, 11.02) * mm});
            skLineSegment(sketch, "E428", {"start": v(-6.56, 11.02) * mm, "end": v(-6.58, 10.76) * mm});
            skLineSegment(sketch, "E429", {"start": v(-6.58, 10.76) * mm, "end": v(-6.6, 10.51) * mm});
            skLineSegment(sketch, "E430", {"start": v(-6.6, 10.51) * mm, "end": v(-6.6, 10.28) * mm});
            skLineSegment(sketch, "E431", {"start": v(-6.6, 10.28) * mm, "end": v(-6.6, 10.05) * mm});
            skLineSegment(sketch, "E432", {"start": v(-6.6, 10.05) * mm, "end": v(-6.58, 9.84) * mm});
            skLineSegment(sketch, "E433", {"start": v(-6.58, 9.84) * mm, "end": v(-6.57, 9.64) * mm});
            skLineSegment(sketch, "E434", {"start": v(-6.57, 9.64) * mm, "end": v(-6.55, 9.45) * mm});
            skLineSegment(sketch, "E435", {"start": v(-6.55, 9.45) * mm, "end": v(-6.52, 9.28) * mm});
            skLineSegment(sketch, "E436", {"start": v(-6.52, 9.28) * mm, "end": v(-6.49, 9.12) * mm});
            skLineSegment(sketch, "E437", {"start": v(-6.49, 9.12) * mm, "end": v(-6.45, 8.97) * mm});
            skLineSegment(sketch, "E438", {"start": v(-6.45, 8.97) * mm, "end": v(-6.42, 8.84) * mm});
            skLineSegment(sketch, "E439", {"start": v(-6.42, 8.84) * mm, "end": v(-6.38, 8.72) * mm});
            skLineSegment(sketch, "E440", {"start": v(-6.38, 8.72) * mm, "end": v(-6.35, 8.61) * mm});
            skLineSegment(sketch, "E441", {"start": v(-6.35, 8.61) * mm, "end": v(-6.31, 8.52) * mm});
            skLineSegment(sketch, "E442", {"start": v(-6.31, 8.52) * mm, "end": v(-6.28, 8.44) * mm});
            skLineSegment(sketch, "E443", {"start": v(-6.28, 8.44) * mm, "end": v(-6.25, 8.37) * mm});
            skLineSegment(sketch, "E444", {"start": v(-6.25, 8.37) * mm, "end": v(-6.22, 8.32) * mm});
            skLineSegment(sketch, "E445", {"start": v(-6.22, 8.32) * mm, "end": v(-6.2, 8.27) * mm});
            skLineSegment(sketch, "E446", {"start": v(-6.2, 8.27) * mm, "end": v(-6.17, 8.24) * mm});
            skLineSegment(sketch, "E447", {"start": v(-6.17, 8.24) * mm, "end": v(-6.16, 8.22) * mm});
            skLineSegment(sketch, "E448", {"start": v(-6.16, 8.22) * mm, "end": v(-6.15, 8.2) * mm});
            skLineSegment(sketch, "E449", {"start": v(-6.15, 8.2) * mm, "end": v(-5.04, 6.73) * mm});
            skLineSegment(sketch, "E450", {"start": v(-5.04, 6.73) * mm, "end": v(-6.76, 5) * mm});
            skLineSegment(sketch, "E451", {"start": v(-6.76, 5) * mm, "end": v(-8.25, 6.1) * mm});
            skLineSegment(sketch, "E452", {"start": v(-8.25, 6.1) * mm, "end": v(-8.26, 6.1) * mm});
            skLineSegment(sketch, "E453", {"start": v(-8.26, 6.1) * mm, "end": v(-8.28, 6.12) * mm});
            skLineSegment(sketch, "E454", {"start": v(-8.28, 6.12) * mm, "end": v(-8.32, 6.14) * mm});
            skLineSegment(sketch, "E455", {"start": v(-8.32, 6.14) * mm, "end": v(-8.36, 6.16) * mm});
            skLineSegment(sketch, "E456", {"start": v(-8.36, 6.16) * mm, "end": v(-8.42, 6.19) * mm});
            skLineSegment(sketch, "E457", {"start": v(-8.42, 6.19) * mm, "end": v(-8.48, 6.22) * mm});
            skLineSegment(sketch, "E458", {"start": v(-8.48, 6.22) * mm, "end": v(-8.57, 6.25) * mm});
            skLineSegment(sketch, "E459", {"start": v(-8.57, 6.25) * mm, "end": v(-8.66, 6.29) * mm});
            skLineSegment(sketch, "E460", {"start": v(-8.66, 6.29) * mm, "end": v(-8.77, 6.32) * mm});
            skLineSegment(sketch, "E461", {"start": v(-8.77, 6.32) * mm, "end": v(-8.89, 6.36) * mm});
            skLineSegment(sketch, "E462", {"start": v(-8.89, 6.36) * mm, "end": v(-9.02, 6.4) * mm});
            skLineSegment(sketch, "E463", {"start": v(-9.02, 6.4) * mm, "end": v(-9.17, 6.42) * mm});
            skLineSegment(sketch, "E464", {"start": v(-9.17, 6.42) * mm, "end": v(-9.33, 6.45) * mm});
            skLineSegment(sketch, "E465", {"start": v(-9.33, 6.45) * mm, "end": v(-9.5, 6.48) * mm});
            skLineSegment(sketch, "E466", {"start": v(-9.5, 6.48) * mm, "end": v(-9.68, 6.5) * mm});
            skLineSegment(sketch, "E467", {"start": v(-9.68, 6.5) * mm, "end": v(-9.88, 6.52) * mm});
            skLineSegment(sketch, "E468", {"start": v(-9.88, 6.52) * mm, "end": v(-10.1, 6.52) * mm});
            skLineSegment(sketch, "E469", {"start": v(-10.1, 6.52) * mm, "end": v(-10.32, 6.53) * mm});
            skLineSegment(sketch, "E470", {"start": v(-10.32, 6.53) * mm, "end": v(-10.56, 6.52) * mm});
            skLineSegment(sketch, "E471", {"start": v(-10.56, 6.52) * mm, "end": v(-10.8, 6.5) * mm});
            skLineSegment(sketch, "E472", {"start": v(-10.8, 6.5) * mm, "end": v(-11.07, 6.48) * mm});
            skLineSegment(sketch, "E473", {"start": v(-11.07, 6.48) * mm, "end": v(-11.34, 6.44) * mm});
            skLineSegment(sketch, "E474", {"start": v(-11.34, 6.44) * mm, "end": v(-11.48, 6.31) * mm});
            skLineSegment(sketch, "E475", {"start": v(-11.48, 6.31) * mm, "end": v(-11.9, 5.5) * mm});
            skLineSegment(sketch, "E476", {"start": v(-11.9, 5.5) * mm, "end": v(-11.92, 5.3) * mm});
            skLineSegment(sketch, "E477", {"start": v(-11.92, 5.3) * mm, "end": v(-11.78, 5.06) * mm});
            skLineSegment(sketch, "E478", {"start": v(-11.78, 5.06) * mm, "end": v(-11.65, 4.84) * mm});
            skLineSegment(sketch, "E479", {"start": v(-11.65, 4.84) * mm, "end": v(-11.51, 4.63) * mm});
            skLineSegment(sketch, "E480", {"start": v(-11.51, 4.63) * mm, "end": v(-11.38, 4.43) * mm});
            skLineSegment(sketch, "E481", {"start": v(-11.38, 4.43) * mm, "end": v(-11.24, 4.25) * mm});
            skLineSegment(sketch, "E482", {"start": v(-11.24, 4.25) * mm, "end": v(-11.1, 4.09) * mm});
            skLineSegment(sketch, "E483", {"start": v(-11.1, 4.09) * mm, "end": v(-10.98, 3.94) * mm});
            skLineSegment(sketch, "E484", {"start": v(-10.98, 3.94) * mm, "end": v(-10.85, 3.8) * mm});
            skLineSegment(sketch, "E485", {"start": v(-10.85, 3.8) * mm, "end": v(-10.73, 3.68) * mm});
            skLineSegment(sketch, "E486", {"start": v(-10.73, 3.68) * mm, "end": v(-10.6, 3.56) * mm});
            skLineSegment(sketch, "E487", {"start": v(-10.6, 3.56) * mm, "end": v(-10.5, 3.47) * mm});
            skLineSegment(sketch, "E488", {"start": v(-10.5, 3.47) * mm, "end": v(-10.39, 3.38) * mm});
            skLineSegment(sketch, "E489", {"start": v(-10.39, 3.38) * mm, "end": v(-10.3, 3.3) * mm});
            skLineSegment(sketch, "E490", {"start": v(-10.3, 3.3) * mm, "end": v(-10.2, 3.24) * mm});
            skLineSegment(sketch, "E491", {"start": v(-10.2, 3.24) * mm, "end": v(-10.11, 3.18) * mm});
            skLineSegment(sketch, "E492", {"start": v(-10.11, 3.18) * mm, "end": v(-10.04, 3.14) * mm});
            skLineSegment(sketch, "E493", {"start": v(-10.04, 3.14) * mm, "end": v(-9.97, 3.1) * mm});
            skLineSegment(sketch, "E494", {"start": v(-9.97, 3.1) * mm, "end": v(-9.92, 3.07) * mm});
            skLineSegment(sketch, "E495", {"start": v(-9.92, 3.07) * mm, "end": v(-9.87, 3.05) * mm});
            skLineSegment(sketch, "E496", {"start": v(-9.87, 3.05) * mm, "end": v(-9.84, 3.04) * mm});
            skLineSegment(sketch, "E497", {"start": v(-9.84, 3.04) * mm, "end": v(-9.82, 3.03) * mm});
            skLineSegment(sketch, "E498", {"start": v(-9.82, 3.03) * mm, "end": v(-9.8, 3.02) * mm});
            skLineSegment(sketch, "E499", {"start": v(-9.8, 3.02) * mm, "end": v(-8.03, 2.48) * mm});
            skLineSegment(sketch, "E500", {"start": v(-8.03, 2.48) * mm, "end": v(-8.4, 0.07) * mm});
            skCircle(sketch, "E501", {"center": v(0, 0) * mm, "radius": 10.92 * mm, "construction": true});
            skSolve(sketch);
        }
        {
            var Q0;
            Q0 = qSketchRegion(id + "F0", true);
            extrude(context, id + "F1", {"entities" : qUnion([Q0]), "depth" : 8 * mm, "offsetDistance" : 25 * mm});
        }
    });
